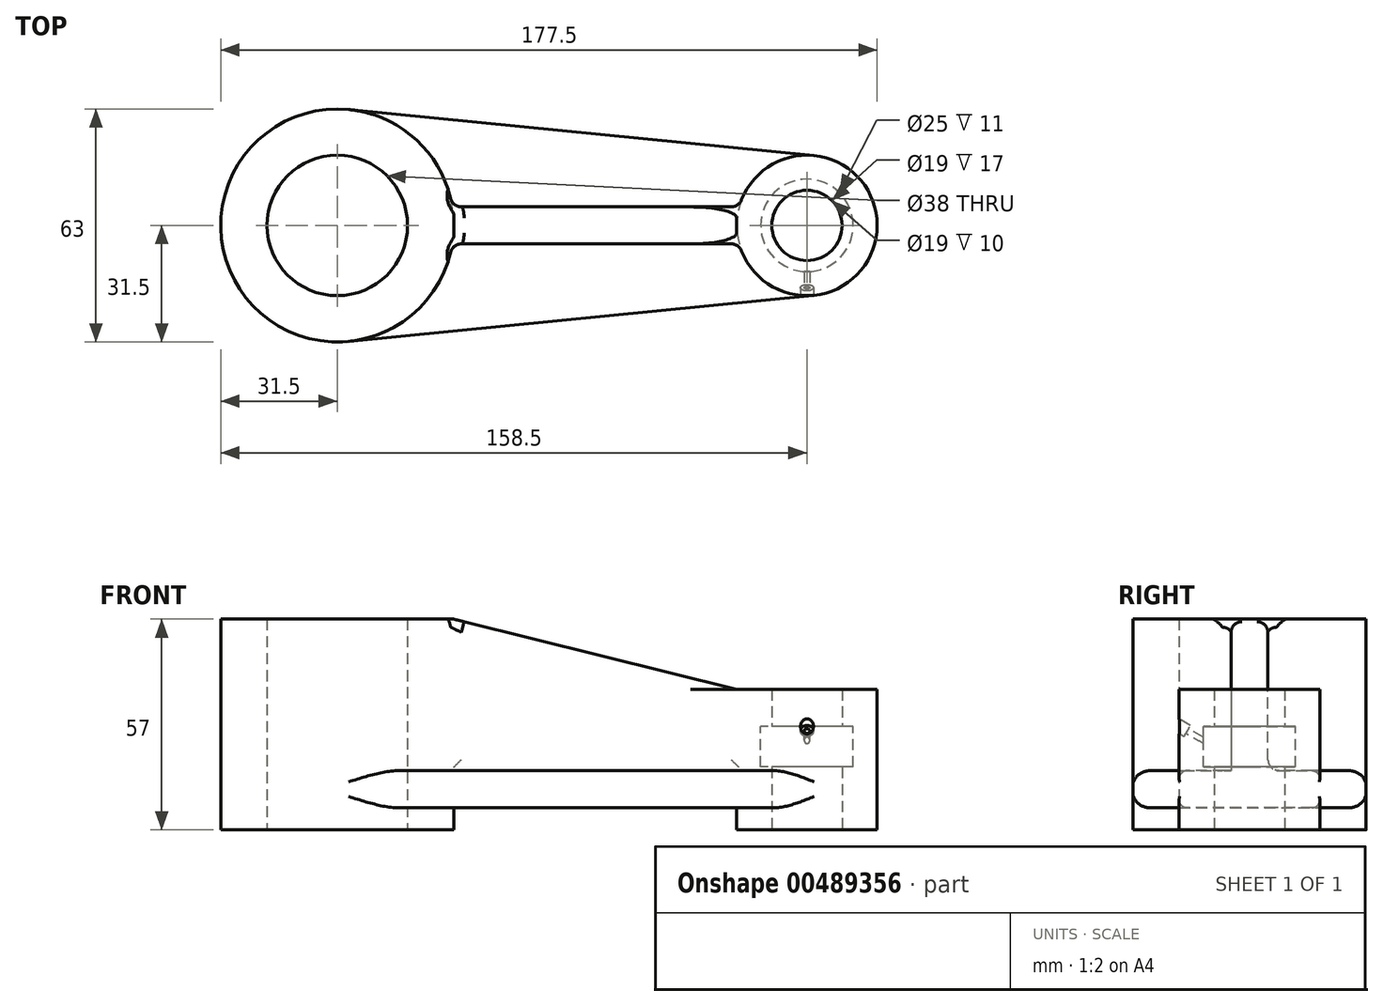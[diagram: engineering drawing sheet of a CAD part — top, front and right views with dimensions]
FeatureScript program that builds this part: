
annotation { "Feature Type Name" : "Feature", "Feature Type Description" : "" }
export const myFeature = defineFeature(function(context is Context, id is Id, definition is map)
    precondition{}
    {
        {
            var Q0;
            Q0=qCreatedBy(makeId("Top.planeOp"),FACE);
            var sketch = newSketch(context, id + "F0", { "sketchPlane" : qUnion([Q0])});
            skLineSegment(sketch, "E0", {"start": v(0, 0) * mm, "end": v(-127, 0) * mm, "construction": true});
            skCircle(sketch, "E1", {"center": v(-127, 0) * mm, "radius": 19 * mm});
            skCircle(sketch, "E2", {"center": v(0, 0) * mm, "radius": 9.5 * mm});
            skCircle(sketch, "E3", {"center": v(-127, 0) * mm, "radius": 31.5 * mm});
            skCircle(sketch, "E4", {"center": v(0, 0) * mm, "radius": 19 * mm});
            skLineSegment(sketch, "E5", {"start": v(-123.9, 31.35) * mm, "end": v(1.87, 18.9) * mm});
            skLineSegment(sketch, "E6", {"start": v(-123.9, -31.35) * mm, "end": v(1.87, -18.9) * mm});
            skSolve(sketch);
        }
        {
            var Q0;
            Q0=makeQuery(id+"F0.imprint","IMPRINT",FACE,{"disambiguationData":[TD([[makeQuery(id+"F0.imprint","IMPRINT",EDGE,{"derivedFrom":sQuery(id+"F0.wireOp",EDGE,"E1")}),-1.0]])]});
            extrude(context, id + "F1", {"entities" : qUnion([Q0]), "depth" : 51 * mm, "offsetDistance" : 25 * mm});
        }
        {
            var Q0;
            {var subQ0=sQuery(id+"F0.wireOp",EDGE,"E5");Q0=makeQuery(id+"F0.imprint","IMPRINT",FACE,{"disambiguationData":[TD([[makeQuery(id+"F0.imprint","IMPRINT",EDGE,{"derivedFrom":subQ0}),-1.0]])]});}
            extrude(context, id + "F2", {"entities" : qUnion([Q0]), "operationType" : NewBodyOperationType.ADD, "depth" : 10 * mm, "offsetDistance" : 25 * mm});
        }
        {
            var Q0;
            Q0=makeQuery(id+"F0.imprint","IMPRINT",FACE,{"disambiguationData":[TD([[makeQuery(id+"F0.imprint","IMPRINT",EDGE,{"derivedFrom":sQuery(id+"F0.wireOp",EDGE,"E2")}),-1.0]])]});
            extrude(context, id + "F3", {"entities" : qUnion([Q0]), "operationType" : NewBodyOperationType.ADD, "depth" : 32 * mm, "offsetDistance" : 25 * mm});
        }
        {
            var Q0;
            Q0=makeQuery(id+"F0.imprint","IMPRINT",FACE,{"disambiguationData":[TD([[makeQuery(id+"F0.imprint","IMPRINT",EDGE,{"derivedFrom":sQuery(id+"F0.wireOp",EDGE,"E1")}),-1.0]])]});
            extrude(context, id + "F4", {"entities" : qUnion([Q0]), "operationType" : NewBodyOperationType.ADD, "oppositeDirection" : true, "depth" : 6 * mm, "offsetDistance" : 25 * mm});
        }
        {
            var Q0;
            Q0=makeQuery(id+"F0.imprint","IMPRINT",FACE,{"disambiguationData":[TD([[makeQuery(id+"F0.imprint","IMPRINT",EDGE,{"derivedFrom":sQuery(id+"F0.wireOp",EDGE,"E2")}),-1.0]])]});
            extrude(context, id + "F5", {"entities" : qUnion([Q0]), "operationType" : NewBodyOperationType.ADD, "oppositeDirection" : true, "depth" : 6 * mm, "offsetDistance" : 25 * mm});
        }
        {
            var Q0;
            Q0=qCreatedBy(makeId("Front.planeOp"),FACE);
            var sketch = newSketch(context, id + "F6", { "sketchPlane" : qUnion([Q0])});
            skLineSegment(sketch, "E7.0", {"start": v(-158.5, 51) * mm, "end": v(-95.5, 51) * mm, "construction": true});
            skLineSegment(sketch, "E8.0", {"start": v(-19, 32) * mm, "end": v(19, 32) * mm, "construction": true});
            skLineSegment(sketch, "E9", {"start": v(-107.3, 51) * mm, "end": v(-107.3, 10) * mm});
            skLineSegment(sketch, "E10", {"start": v(-107.3, 10) * mm, "end": v(-15.3, 10) * mm});
            skLineSegment(sketch, "E11", {"start": v(-15.3, 10) * mm, "end": v(-15.3, 32) * mm});
            skLineSegment(sketch, "E12", {"start": v(-15.3, 32) * mm, "end": v(-19, 32) * mm});
            skLineSegment(sketch, "E13", {"start": v(-95.5, 51) * mm, "end": v(-107.3, 51) * mm});
            skLineSegment(sketch, "E14", {"start": v(-95.5, 51) * mm, "end": v(-19, 32) * mm});
            skSolve(sketch);
        }
        {
            var Q0;
            Q0=qCreatedBy(makeId("Front.planeOp"),FACE);
            var sketch = newSketch(context, id + "F7", { "sketchPlane" : qUnion([Q0])});
            skLineSegment(sketch, "E15", {"start": v(0, 0) * mm, "end": v(0, 41.96) * mm, "construction": true});
            skLineSegment(sketch, "E16.bottom", {"start": v(0, 11) * mm, "end": v(12.5, 11) * mm});
            skLineSegment(sketch, "E16.top", {"start": v(0, 22) * mm, "end": v(12.5, 22) * mm});
            skLineSegment(sketch, "E16.left", {"start": v(0, 11) * mm, "end": v(0, 22) * mm});
            skLineSegment(sketch, "E16.right", {"start": v(12.5, 11) * mm, "end": v(12.5, 22) * mm});
            skSolve(sketch);
        }
        {
            var Q0;
            Q0 = qSketchRegion(id + "F7", true);
            var Q1;
            Q1=sQuery(id+"F7.wireOp",EDGE,"E15");
            revolve(context, id + "F8", {"operationType" : NewBodyOperationType.REMOVE, "entities" : qUnion([Q0]), "axis" : qUnion([Q1]), "revolveType" : RevolveType.FULL, "oppositeDirection" : true});
        }
        {
            var Q0;
            Q0=qCreatedBy(makeId("Front.planeOp"),FACE);
            cPlane(context, id + "F9", {"entities" : qUnion([Q0]), "cplaneType" : CPlaneType.OFFSET, "offset" : 19 * mm, "width" : 150 * mm, "height" : 150 * mm});
        }
        {
            var Q0;
            Q0=qCreatedBy(id+"F9.planeOp",FACE);
            var sketch = newSketch(context, id + "F10", { "sketchPlane" : qUnion([Q0])});
            skLineSegment(sketch, "E17.0", {"start": v(0, 22) * mm, "end": v(12.5, 22) * mm, "construction": true});
            skSolve(sketch);
        }
        {
            var Q0;
            Q0=qCreatedBy(id+"F9.planeOp",FACE);
            var Q1;
            Q1=sQuery(id+"F10.wireOp",EDGE,"E17.0");
            cPlane(context, id + "F11", {"entities" : qUnion([Q0, Q1]), "cplaneType" : CPlaneType.LINE_ANGLE, "offset" : 25 * mm, "angle" : 30 * degree, "oppositeDirection" : true, "width" : 150 * mm, "height" : 150 * mm});
        }
        {
            var Q0;
            Q0=qCreatedBy(id+"F11.planeOp",FACE);
            var sketch = newSketch(context, id + "F12", { "sketchPlane" : qUnion([Q0])});
            skPoint(sketch, "E18.0", {"position": v(0, 9.55) * mm});
            skCircle(sketch, "E19", {"center": v(0, 9.55) * mm, "radius": 0.75 * mm});
            skCircle(sketch, "E20", {"center": v(0, 9.55) * mm, "radius": 1.75 * mm});
            skSolve(sketch);
        }
        {
            var Q0;
            Q0=makeQuery(id+"F12.imprint","IMPRINT",FACE,{"disambiguationData":[TD([[makeQuery(id+"F12.imprint","IMPRINT",EDGE,{"derivedFrom":sQuery(id+"F12.wireOp",EDGE,"E19")}),1.0]])]});
            extrude(context, id + "F13", {"entities" : qUnion([Q0]), "operationType" : NewBodyOperationType.REMOVE, "endBound" : BoundingType.SYMMETRIC, "depth" : 19 * mm, "offsetDistance" : 25 * mm});
        }
        {
            var Q0;
            Q0 = qSketchRegion(id + "F12", true);
            extrude(context, id + "F14", {"entities" : qUnion([Q0]), "operationType" : NewBodyOperationType.REMOVE, "endBound" : BoundingType.SYMMETRIC, "depth" : 5 * mm, "offsetDistance" : 25 * mm});
        }
        {
            var Q0;
            Q0 = qSketchRegion(id + "F6", true);
            extrude(context, id + "F15", {"entities" : qUnion([Q0]), "operationType" : NewBodyOperationType.ADD, "endBound" : BoundingType.SYMMETRIC, "depth" : 10 * mm, "offsetDistance" : 25 * mm});
        }
        {
            var Q0;
            {var subQ0=sQuery(id+"F0.wireOp",EDGE,"E4");var subQ1=sQuery(id+"F0.wireOp",EDGE,"E5");Q0=makeQuery(id+"F15.boolean.opBoolean","SPLIT",EDGE,{"disambiguationData":[TD([makeQuery(id+"F2.opExtrude","SWEPT_FACE",FACE,{"disambiguationData":[OSD([subQ1])]})])],"derivedFrom":makeQuery(id+"F2.opExtrude","CAP_EDGE",EDGE,{"disambiguationData":[OSD([subQ0])],"isStart":false})});}
            var Q1;
            {var subQ0=sQuery(id+"F0.wireOp",EDGE,"E4");var subQ1=sQuery(id+"F0.wireOp",EDGE,"E6");Q1=makeQuery(id+"F15.boolean.opBoolean","SPLIT",EDGE,{"disambiguationData":[TD([makeQuery(id+"F2.opExtrude","SWEPT_FACE",FACE,{"disambiguationData":[OSD([subQ1])]})])],"derivedFrom":makeQuery(id+"F2.opExtrude","CAP_EDGE",EDGE,{"disambiguationData":[OSD([subQ0])],"isStart":false})});}
            var Q2;
            Q2=makeQuery(id+"F2.opExtrude","CAP_EDGE",EDGE,{"disambiguationData":[OSD([sQuery(id+"F0.wireOp",EDGE,"E6")])],"isStart":false});
            var Q3;
            {var subQ0=sQuery(id+"F0.wireOp",EDGE,"E5");var subQ1=sQuery(id+"F0.wireOp",EDGE,"E3");Q3=makeQuery(id+"F15.boolean.opBoolean","SPLIT",EDGE,{"disambiguationData":[TD([makeQuery(id+"F2.opExtrude","SWEPT_FACE",FACE,{"disambiguationData":[OSD([subQ0])]})])],"derivedFrom":makeQuery(id+"F2.opExtrude","CAP_EDGE",EDGE,{"disambiguationData":[OSD([subQ1])],"isStart":false})});}
            var Q4;
            {var subQ0=sQuery(id+"F0.wireOp",EDGE,"E6");var subQ1=sQuery(id+"F0.wireOp",EDGE,"E3");Q4=makeQuery(id+"F15.boolean.opBoolean","SPLIT",EDGE,{"disambiguationData":[TD([makeQuery(id+"F2.opExtrude","SWEPT_FACE",FACE,{"disambiguationData":[OSD([subQ0])]})])],"derivedFrom":makeQuery(id+"F2.opExtrude","CAP_EDGE",EDGE,{"disambiguationData":[OSD([subQ1])],"isStart":false})});}
            var Q5;
            Q5=makeQuery(id+"F2.opExtrude","CAP_EDGE",EDGE,{"disambiguationData":[OSD([sQuery(id+"F0.wireOp",EDGE,"E5")])],"isStart":false});
            var Q6;
            {var subQ0=sQuery(id+"F0.wireOp",EDGE,"E3");Q6=makeQuery(id+"F15.boolean.opBoolean","INTERSECT",EDGE,{"derivedFrom":[makeQuery(id+"F4.boolean.opBoolean","MERGE",FACE,{"derivedFrom":[makeQuery(id+"F1.opExtrude","SWEPT_FACE",FACE,{"disambiguationData":[OSD([subQ0])]}),makeQuery(id+"F4.opExtrude","SWEPT_FACE",FACE,{"disambiguationData":[OSD([subQ0])]})]}),makeQuery(id+"F15.opExtrude","CAP_FACE",FACE,{"disambiguationData":[OSD([sQuery(id+"F6.wireOp",EDGE,"E9"),sQuery(id+"F6.wireOp",EDGE,"E10"),sQuery(id+"F6.wireOp",EDGE,"E11"),sQuery(id+"F6.wireOp",EDGE,"E12"),sQuery(id+"F6.wireOp",EDGE,"E13"),sQuery(id+"F6.wireOp",EDGE,"E14")])],"isStart":false})]});}
            var Q7;
            {var subQ0=sQuery(id+"F0.wireOp",EDGE,"E4");Q7=makeQuery(id+"F15.boolean.opBoolean","INTERSECT",EDGE,{"derivedFrom":[makeQuery(id+"F5.boolean.opBoolean","MERGE",FACE,{"derivedFrom":[makeQuery(id+"F3.opExtrude","SWEPT_FACE",FACE,{"disambiguationData":[OSD([subQ0])]}),makeQuery(id+"F5.opExtrude","SWEPT_FACE",FACE,{"disambiguationData":[OSD([subQ0])]})]}),makeQuery(id+"F15.opExtrude","CAP_FACE",FACE,{"disambiguationData":[OSD([sQuery(id+"F6.wireOp",EDGE,"E9"),sQuery(id+"F6.wireOp",EDGE,"E10"),sQuery(id+"F6.wireOp",EDGE,"E11"),sQuery(id+"F6.wireOp",EDGE,"E12"),sQuery(id+"F6.wireOp",EDGE,"E13"),sQuery(id+"F6.wireOp",EDGE,"E14")])],"isStart":false})]});}
            var Q8;
            {var subQ0=sQuery(id+"F0.wireOp",EDGE,"E3");Q8=makeQuery(id+"F15.boolean.opBoolean","INTERSECT",EDGE,{"derivedFrom":[makeQuery(id+"F4.boolean.opBoolean","MERGE",FACE,{"derivedFrom":[makeQuery(id+"F1.opExtrude","SWEPT_FACE",FACE,{"disambiguationData":[OSD([subQ0])]}),makeQuery(id+"F4.opExtrude","SWEPT_FACE",FACE,{"disambiguationData":[OSD([subQ0])]})]}),makeQuery(id+"F15.opExtrude","CAP_FACE",FACE,{"disambiguationData":[OSD([sQuery(id+"F6.wireOp",EDGE,"E9"),sQuery(id+"F6.wireOp",EDGE,"E10"),sQuery(id+"F6.wireOp",EDGE,"E11"),sQuery(id+"F6.wireOp",EDGE,"E12"),sQuery(id+"F6.wireOp",EDGE,"E13"),sQuery(id+"F6.wireOp",EDGE,"E14")])],"isStart":true})]});}
            var Q9;
            {var subQ0=sQuery(id+"F0.wireOp",EDGE,"E4");Q9=makeQuery(id+"F15.boolean.opBoolean","INTERSECT",EDGE,{"derivedFrom":[makeQuery(id+"F5.boolean.opBoolean","MERGE",FACE,{"derivedFrom":[makeQuery(id+"F3.opExtrude","SWEPT_FACE",FACE,{"disambiguationData":[OSD([subQ0])]}),makeQuery(id+"F5.opExtrude","SWEPT_FACE",FACE,{"disambiguationData":[OSD([subQ0])]})]}),makeQuery(id+"F15.opExtrude","CAP_FACE",FACE,{"disambiguationData":[OSD([sQuery(id+"F6.wireOp",EDGE,"E9"),sQuery(id+"F6.wireOp",EDGE,"E10"),sQuery(id+"F6.wireOp",EDGE,"E11"),sQuery(id+"F6.wireOp",EDGE,"E12"),sQuery(id+"F6.wireOp",EDGE,"E13"),sQuery(id+"F6.wireOp",EDGE,"E14")])],"isStart":true})]});}
            var Q10;
            Q10=makeQuery(id+"F15.opExtrude","CAP_EDGE",EDGE,{"disambiguationData":[OSD([sQuery(id+"F6.wireOp",EDGE,"E10")])],"isStart":true});
            var Q11;
            Q11=makeQuery(id+"F15.opExtrude","CAP_EDGE",EDGE,{"disambiguationData":[OSD([sQuery(id+"F6.wireOp",EDGE,"E10")])],"isStart":false});
            var Q12;
            Q12=makeQuery(id+"F2.opExtrude","CAP_EDGE",EDGE,{"disambiguationData":[OSD([sQuery(id+"F0.wireOp",EDGE,"E6")])],"isStart":true});
            var Q13;
            Q13=makeQuery(id+"F2.opExtrude","CAP_EDGE",EDGE,{"disambiguationData":[OSD([sQuery(id+"F0.wireOp",EDGE,"E5")])],"isStart":true});
            fillet(context, id + "F16", {"entities" : qUnion([Q0, Q1, Q2, Q3, Q4, Q5, Q6, Q7, Q8, Q9, Q10, Q11, Q12, Q13]), "radius" : 3 * mm, "tangentPropagation" : true, "allowEdgeOverflow" : false});
        }
        {
            var Q0;
            Q0=makeQuery(id+"F15.opExtrude","CAP_EDGE",EDGE,{"disambiguationData":[OSD([sQuery(id+"F6.wireOp",EDGE,"E14")])],"isStart":false});
            var Q1;
            Q1=makeQuery(id+"F15.opExtrude","CAP_EDGE",EDGE,{"disambiguationData":[OSD([sQuery(id+"F6.wireOp",EDGE,"E14")])],"isStart":true});
            fillet(context, id + "F17", {"entities" : qUnion([Q0, Q1]), "radius" : 3 * mm, "tangentPropagation" : true, "allowEdgeOverflow" : false});
        }
    });
